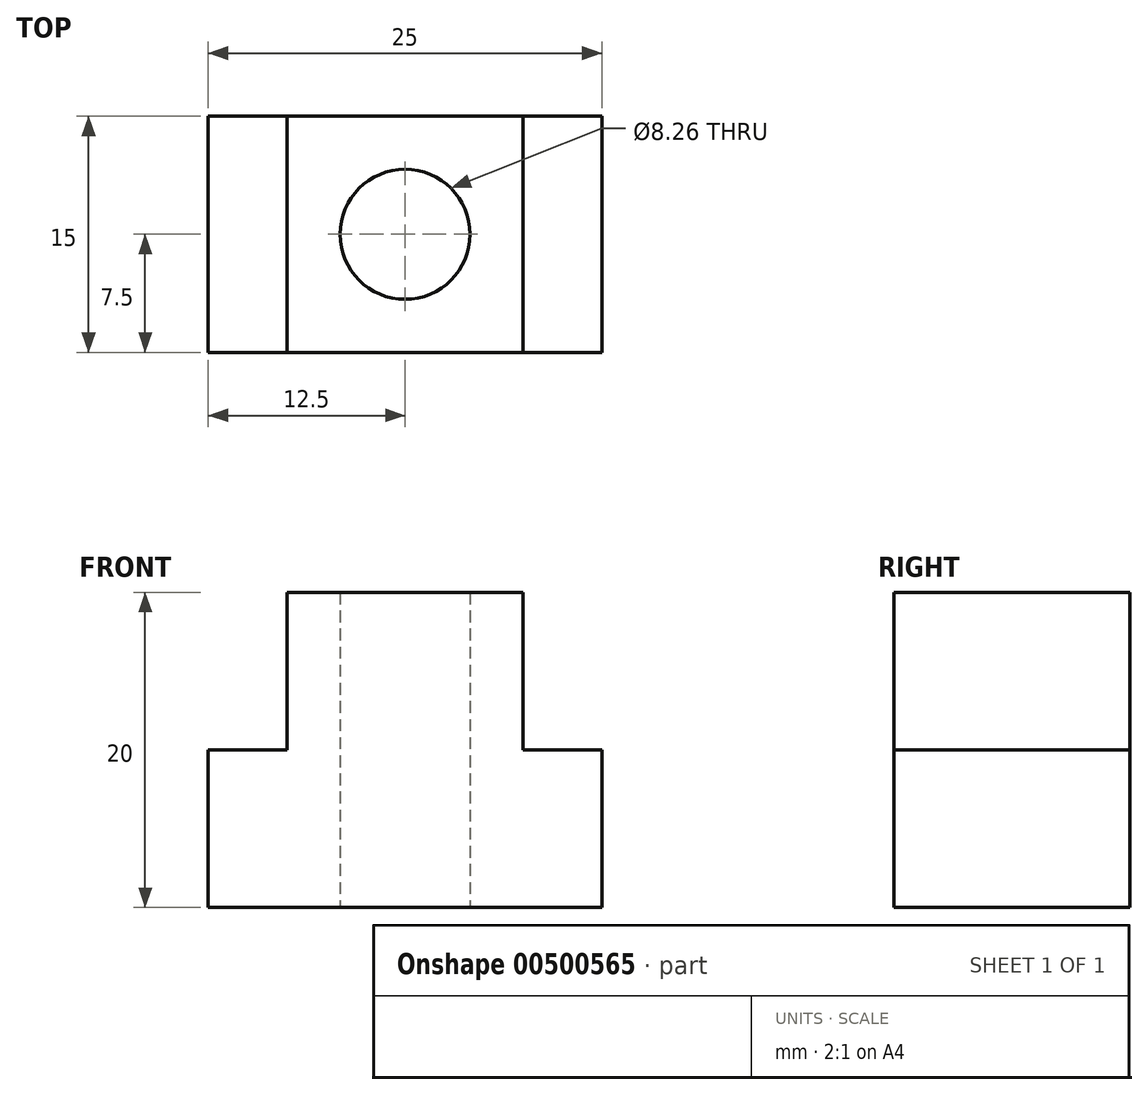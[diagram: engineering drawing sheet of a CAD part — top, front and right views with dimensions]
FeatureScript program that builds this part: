
annotation { "Feature Type Name" : "Feature", "Feature Type Description" : "" }
export const myFeature = defineFeature(function(context is Context, id is Id, definition is map)
    precondition{}
    {
        {
            var Q0;
            Q0=qCreatedBy(makeId("Top.planeOp"),FACE);
            var sketch = newSketch(context, id + "F0", { "sketchPlane" : qUnion([Q0])});
            skLineSegment(sketch, "E0.bottom", {"start": v(12.5, 7.5) * mm, "end": v(-12.5, 7.5) * mm});
            skLineSegment(sketch, "E0.top", {"start": v(12.5, -7.5) * mm, "end": v(-12.5, -7.5) * mm});
            skLineSegment(sketch, "E0.left", {"start": v(12.5, 7.5) * mm, "end": v(12.5, -7.5) * mm});
            skLineSegment(sketch, "E0.right", {"start": v(-12.5, 7.5) * mm, "end": v(-12.5, -7.5) * mm});
            skPoint(sketch, "E0.middle", {"position": v(0, 0) * mm});
            skLineSegment(sketch, "E1.bottom", {"start": v(7.5, 7.5) * mm, "end": v(-7.5, 7.5) * mm});
            skLineSegment(sketch, "E1.top", {"start": v(7.5, -7.5) * mm, "end": v(-7.5, -7.5) * mm});
            skLineSegment(sketch, "E1.left", {"start": v(7.5, 7.5) * mm, "end": v(7.5, -7.5) * mm});
            skLineSegment(sketch, "E1.right", {"start": v(-7.5, 7.5) * mm, "end": v(-7.5, -7.5) * mm});
            skCircle(sketch, "E2", {"center": v(0, 0) * mm, "radius": 4.13 * mm});
            skSolve(sketch);
        }
        {
            var Q0;
            {var subQ1=sQuery(id+"F0.wireOp",EDGE,"E1.left");Q0=makeQuery(id+"F0.imprint","IMPRINT",FACE,{"disambiguationData":[TD([[makeQuery(id+"F0.imprint","IMPRINT",EDGE,{"derivedFrom":subQ1}),-1.0]])]});}
            extrude(context, id + "F1", {"entities" : qUnion([Q0]), "depth" : 20 * mm});
        }
        {
            var Q0;
            {var subQ2=sQuery(id+"F0.wireOp",EDGE,"E0.left");Q0=makeQuery(id+"F0.imprint","IMPRINT",FACE,{"disambiguationData":[TD([[makeQuery(id+"F0.imprint","IMPRINT",EDGE,{"derivedFrom":subQ2}),-1.0]])]});}
            var Q1;
            {var subQ0=sQuery(id+"F0.wireOp",EDGE,"E0.right");Q1=makeQuery(id+"F0.imprint","IMPRINT",FACE,{"disambiguationData":[TD([[makeQuery(id+"F0.imprint","IMPRINT",EDGE,{"derivedFrom":subQ0}),1.0]])]});}
            extrude(context, id + "F2", {"entities" : qUnion([Q0, Q1]), "operationType" : NewBodyOperationType.ADD, "depth" : 10 * mm});
        }
    });
